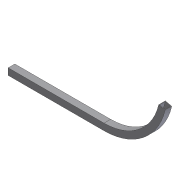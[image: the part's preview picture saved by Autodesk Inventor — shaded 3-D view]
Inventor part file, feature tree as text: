
AUTODESK INVENTOR PART (.ipt)
format: ipt  version: 2012 (Build 160160000, 160)  size: 86,528 bytes
history: native  units: in
note: dims shown in document units (in); Inventor stores cm internally (conversion verified against a paired STEP export)
features: extrude x1, shell x1, sketch x1
ambient origin geometry x8: Origin, YZ Plane, XZ Plane, XY Plane, X Axis, Y Axis, Z Axis, Center Point
bodies: Solid1 (feature_tree)
feature tree (3):
  extrude  "Extrusion1"  Depth=1.0in
  shell  "Shell1"  Thickness=8.5in
  sketch  "Sketch1"  dims[d2=1.0in d3=0.0in d5=1.0in d6=8.5in d7=14.5in d8=0.5277in d9=0.0625in]
